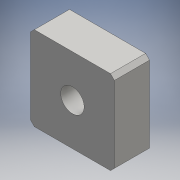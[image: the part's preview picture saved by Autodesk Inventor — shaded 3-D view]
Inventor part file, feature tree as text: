
AUTODESK INVENTOR PART (.ipt)
format: ipt  version: 2016 (Build 200138000, 138)  size: 102,912 bytes
history: native  units: mm
features: chamfer x4, extrude x2, sketch x2, other x1
ambient origin geometry x8: Origin, YZ Plane, XZ Plane, XY Plane, X Axis, Y Axis, Z Axis, Center Point
bodies: Body1 (feature_tree)
feature tree (9):
  other  "ソリッド1"
  extrude  "押し出し1"  Depth=43.0mm
  chamfer  "面取り1"  Distance=43.0mm
  chamfer  "面取り2"  Distance=18.0mm
  chamfer  "面取り3"  Distance=2.0mm Angle=45.0deg
  chamfer  "面取り4"  Distance=2.0mm Angle=45.0deg
  extrude  "押し出し2"  Depth=2.0mm TaperAngle=45.0deg
  sketch  "スケッチ1"
  sketch  "スケッチ2"
